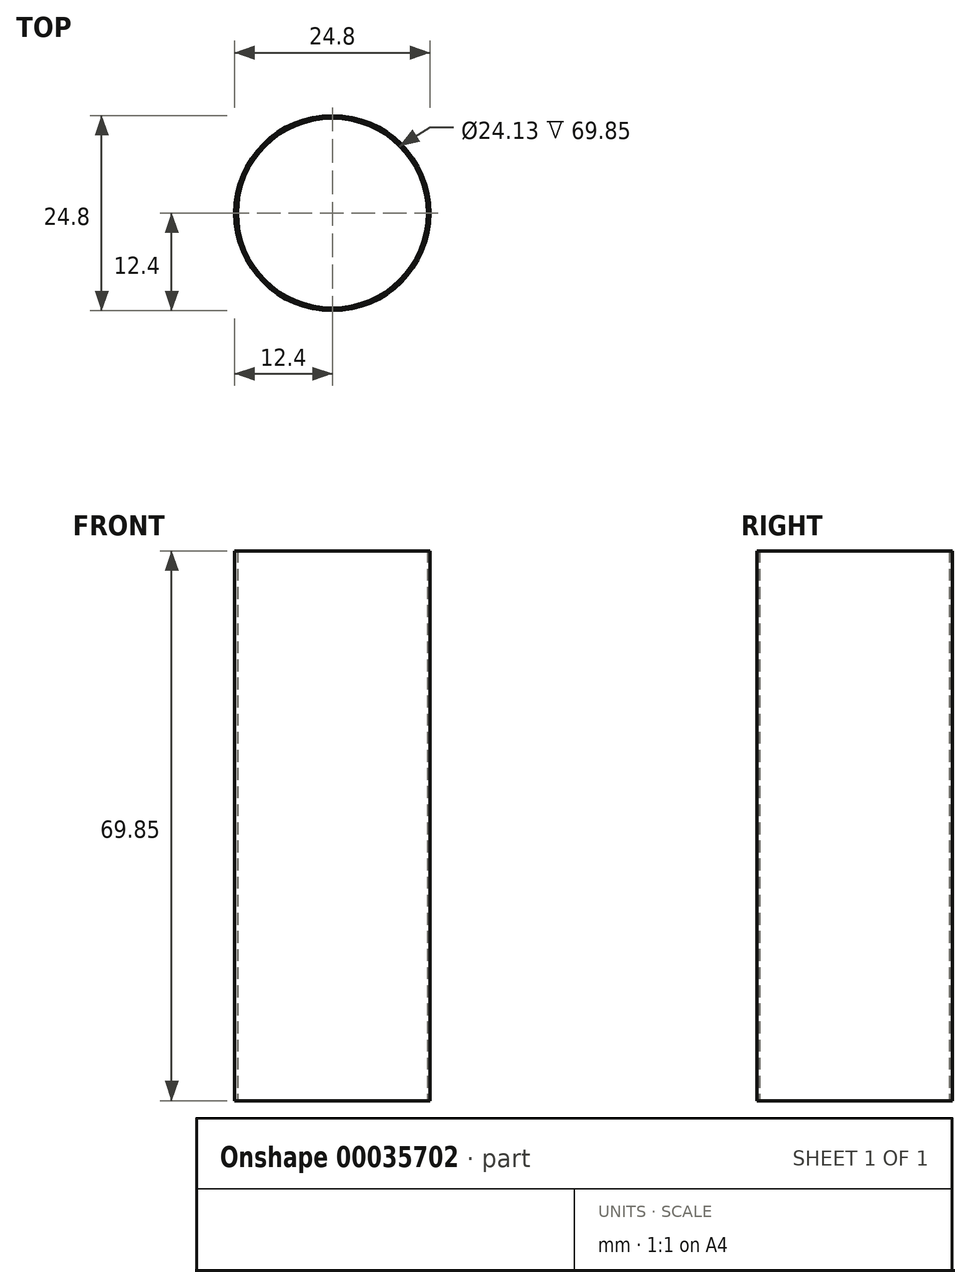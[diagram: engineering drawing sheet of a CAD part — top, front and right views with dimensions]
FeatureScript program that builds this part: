
annotation { "Feature Type Name" : "Feature", "Feature Type Description" : "" }
export const myFeature = defineFeature(function(context is Context, id is Id, definition is map)
    precondition{}
    {
        {
            var Q0;
            Q0=qCreatedBy(makeId("Front.planeOp"),FACE);
            var sketch = newSketch(context, id + "F0", { "sketchPlane" : qUnion([Q0])});
            skLineSegment(sketch, "E0", {"start": v(0, 0) * mm, "end": v(0, 69.85) * mm});
            skLineSegment(sketch, "E1", {"start": v(0, 69.85) * mm, "end": v(12.06, 69.85) * mm});
            skLineSegment(sketch, "E2", {"start": v(12.06, 69.85) * mm, "end": v(12.07, 0) * mm});
            skLineSegment(sketch, "E3", {"start": v(12.07, 0) * mm, "end": v(0, 0) * mm});
            skLineSegment(sketch, "E4", {"start": v(12.07, 0) * mm, "end": v(12.4, 0) * mm});
            skLineSegment(sketch, "E5", {"start": v(12.4, 0) * mm, "end": v(12.4, 69.85) * mm});
            skLineSegment(sketch, "E6", {"start": v(12.4, 69.85) * mm, "end": v(12.07, 69.85) * mm});
            skSolve(sketch);
        }
        {
            var Q0;
            Q0=makeQuery(id+"F0.imprint","IMPRINT",FACE,{"disambiguationData":[TD([[makeQuery(id+"F0.imprint","IMPRINT",EDGE,{"derivedFrom":sQuery(id+"F0.wireOp",EDGE,"E2")}),1.0]])]});
            var Q1;
            Q1=sQuery(id+"F0.wireOp",EDGE,"E0");
            revolve(context, id + "F1", {"entities" : qUnion([Q0]), "axis" : qUnion([Q1]), "revolveType" : RevolveType.FULL});
        }
        {
            var Q0;
            Q0=qCreatedBy(makeId("Top.planeOp"),FACE);
            var sketch = newSketch(context, id + "F2", { "sketchPlane" : qUnion([Q0])});
            skCircle(sketch, "E7.0", {"center": v(0, 0) * mm, "radius": 12.4 * mm});
            skLineSegment(sketch, "E8", {"start": v(0, 0) * mm, "end": v(0, 12.4) * mm});
            skLineSegment(sketch, "E9", {"start": v(0, 0) * mm, "end": v(10.73, -6.2) * mm});
            skLineSegment(sketch, "E10.MirrorCS", {"start": v(0, 0) * mm, "end": v(-10.73, -6.2) * mm});
            skLineSegment(sketch, "E11", {"start": v(0, 0) * mm, "end": v(0, -12.4) * mm});
            skSolve(sketch);
        }
    });
